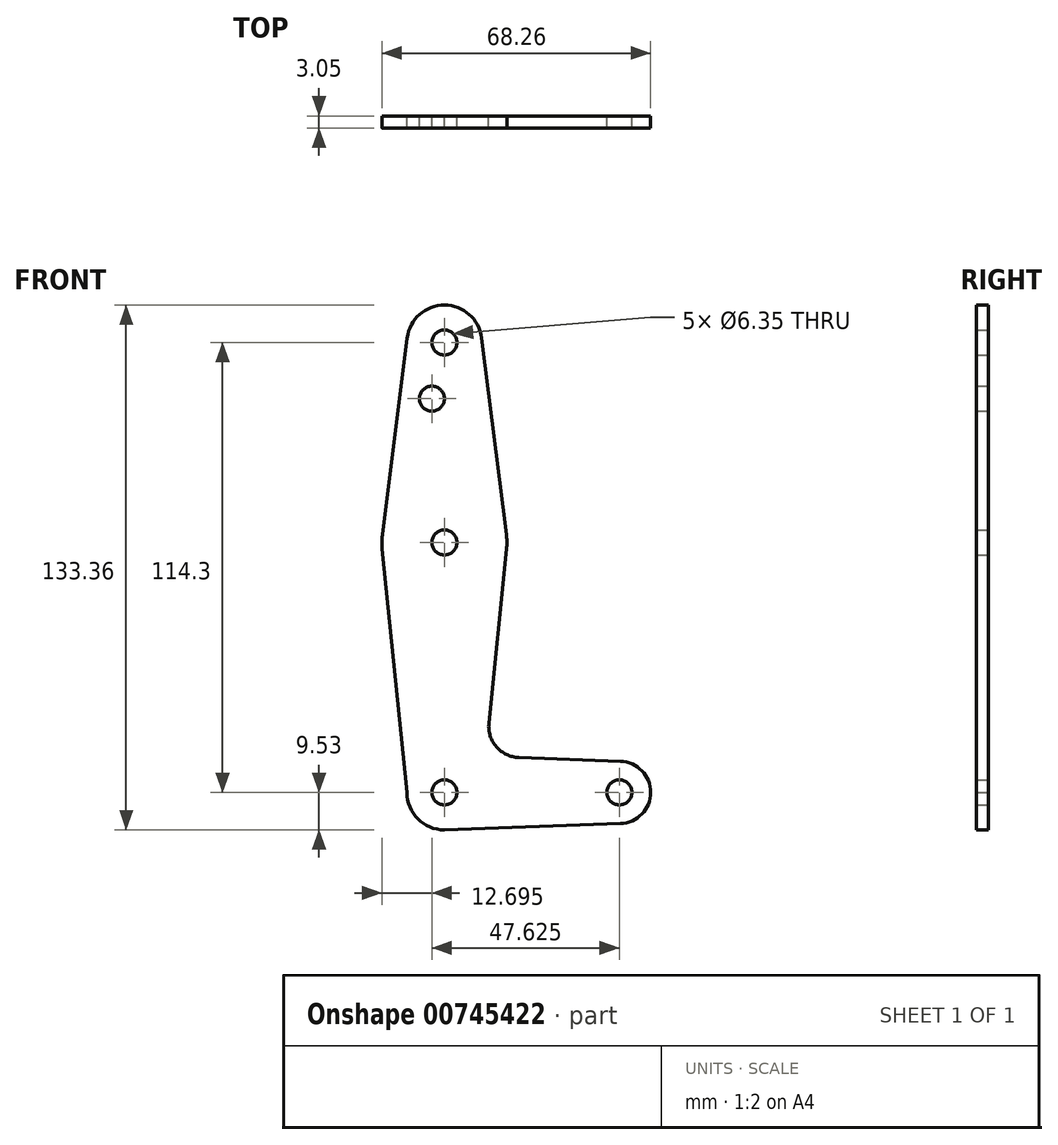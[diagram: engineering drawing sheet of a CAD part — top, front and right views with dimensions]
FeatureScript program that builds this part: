
annotation { "Feature Type Name" : "Feature", "Feature Type Description" : "" }
export const myFeature = defineFeature(function(context is Context, id is Id, definition is map)
    precondition{}
    {
        {
            var Q0;
            Q0=qCreatedBy(makeId("Front.planeOp"),FACE);
            var sketch = newSketch(context, id + "F0", { "sketchPlane" : qUnion([Q0])});
            skLineSegment(sketch, "E0", {"start": v(0, 0) * mm, "end": v(0, 114.3) * mm, "construction": true});
            skLineSegment(sketch, "E1", {"start": v(0, 0) * mm, "end": v(44.45, 0) * mm, "construction": true});
            skCircle(sketch, "E2", {"center": v(0, 114.3) * mm, "radius": 9.53 * mm});
            skCircle(sketch, "E3", {"center": v(0, 63.5) * mm, "radius": 15.88 * mm});
            skCircle(sketch, "E4", {"center": v(0, 0) * mm, "radius": 9.53 * mm});
            skCircle(sketch, "E5", {"center": v(44.45, 0) * mm, "radius": 7.94 * mm});
            skLineSegment(sketch, "E6", {"start": v(-9.45, 115.5) * mm, "end": v(-15.75, 65.48) * mm});
            skLineSegment(sketch, "E7", {"start": v(9.45, 115.5) * mm, "end": v(15.75, 65.48) * mm});
            skLineSegment(sketch, "E8", {"start": v(-9.52, 0) * mm, "end": v(-15.8, 61.9) * mm});
            skLineSegment(sketch, "E9", {"start": v(11.3, 17.6) * mm, "end": v(15.8, 61.9) * mm});
            skLineSegment(sketch, "E10", {"start": v(18.93, 8.85) * mm, "end": v(44.73, 7.93) * mm});
            skLineSegment(sketch, "E11", {"start": v(0, -9.52) * mm, "end": v(44.73, -7.93) * mm});
            skCircle(sketch, "E12", {"center": v(0, 114.3) * mm, "radius": 3.18 * mm});
            skCircle(sketch, "E13", {"center": v(0, 63.5) * mm, "radius": 3.18 * mm});
            skCircle(sketch, "E14", {"center": v(0, 0) * mm, "radius": 3.18 * mm});
            skCircle(sketch, "E15", {"center": v(44.45, 0) * mm, "radius": 3.18 * mm});
            skCircle(sketch, "E16", {"center": v(-3.18, 100.03) * mm, "radius": 3.18 * mm});
            skArc(sketch, "E17.filletArc", {"start": v(11.3, 17.6) * mm, "mid": v(13.22, 11.57) * mm, "end": v(18.93, 8.85) * mm});
            skSolve(sketch);
        }
        {
            var Q0;
            {var subQ0=sQuery(id+"F0.wireOp",EDGE,"E11");var subQ1=sQuery(id+"F0.wireOp",EDGE,"E4");var subQ2=makeQuery(id+"F0.imprint","INTERSECT",VERTEX,{"disambiguationData":[OD(0.0)],"derivedFrom":[subQ1,subQ0]});Q0=makeQuery(id+"F0.imprint","IMPRINT",FACE,{"disambiguationData":[TD([[makeQuery(id+"F0.imprint","IMPRINT",EDGE,{"disambiguationData":[TD([[subQ2,-1.0]])],"derivedFrom":subQ1}),1.0]])]});}
            var Q1;
            Q1=makeQuery(id+"F0.imprint","IMPRINT",FACE,{"disambiguationData":[TD([[makeQuery(id+"F0.imprint","IMPRINT",EDGE,{"derivedFrom":sQuery(id+"F0.wireOp",EDGE,"E12")}),-1.0]])]});
            var Q2;
            Q2=makeQuery(id+"F0.imprint","IMPRINT",FACE,{"disambiguationData":[TD([[makeQuery(id+"F0.imprint","IMPRINT",EDGE,{"derivedFrom":sQuery(id+"F0.wireOp",EDGE,"E15")}),-1.0]])]});
            var Q3;
            Q3=makeQuery(id+"F0.imprint","IMPRINT",FACE,{"disambiguationData":[TD([[makeQuery(id+"F0.imprint","IMPRINT",EDGE,{"derivedFrom":sQuery(id+"F0.wireOp",EDGE,"E13")}),-1.0]])]});
            var Q4;
            {var subQ0=sQuery(id+"F0.wireOp",EDGE,"E8");Q4=makeQuery(id+"F0.imprint","IMPRINT",FACE,{"disambiguationData":[TD([[makeQuery(id+"F0.imprint","IMPRINT",EDGE,{"derivedFrom":subQ0}),-1.0]])]});}
            var Q5;
            Q5=makeQuery(id+"F0.imprint","IMPRINT",FACE,{"disambiguationData":[TD([[makeQuery(id+"F0.imprint","IMPRINT",EDGE,{"derivedFrom":sQuery(id+"F0.wireOp",EDGE,"E14")}),-1.0]])]});
            var Q6;
            {var subQ1=sQuery(id+"F0.wireOp",EDGE,"E6");Q6=makeQuery(id+"F0.imprint","IMPRINT",FACE,{"disambiguationData":[TD([[makeQuery(id+"F0.imprint","IMPRINT",EDGE,{"derivedFrom":subQ1}),1.0]])]});}
            extrude(context, id + "F1", {"entities" : qUnion([Q0, Q1, Q2, Q3, Q4, Q5, Q6]), "depth" : 3.05 * mm, "offsetDistance" : 25.4 * mm});
        }
    });
